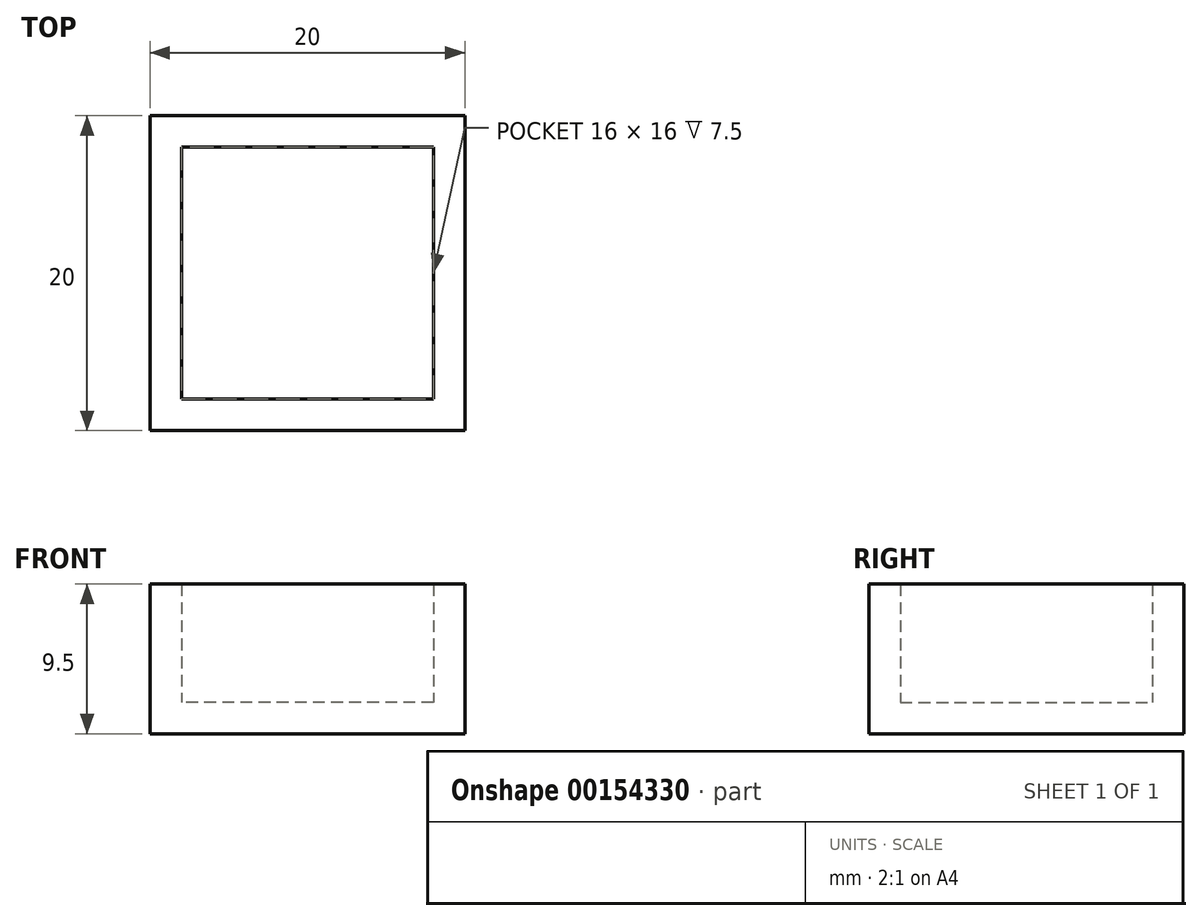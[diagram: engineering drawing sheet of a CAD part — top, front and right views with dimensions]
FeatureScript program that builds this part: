
annotation { "Feature Type Name" : "Feature", "Feature Type Description" : "" }
export const myFeature = defineFeature(function(context is Context, id is Id, definition is map)
    precondition{}
    {
        {
            var Q0;
            Q0=qCreatedBy(makeId("Top.planeOp"),FACE);
            var sketch = newSketch(context, id + "F0", { "sketchPlane" : qUnion([Q0])});
            skLineSegment(sketch, "E0.bottom", {"start": v(10, -10) * mm, "end": v(-10, -10) * mm});
            skLineSegment(sketch, "E0.top", {"start": v(10, 10) * mm, "end": v(-10, 10) * mm});
            skLineSegment(sketch, "E0.left", {"start": v(10, -10) * mm, "end": v(10, 10) * mm});
            skLineSegment(sketch, "E0.right", {"start": v(-10, -10) * mm, "end": v(-10, 10) * mm});
            skPoint(sketch, "E0.middle", {"position": v(0, 0) * mm});
            skLineSegment(sketch, "E1.0", {"start": v(-8, -8) * mm, "end": v(-8, 8) * mm});
            skLineSegment(sketch, "E1.1", {"start": v(8, -8) * mm, "end": v(-8, -8) * mm});
            skLineSegment(sketch, "E1.2", {"start": v(8, -8) * mm, "end": v(8, 8) * mm});
            skLineSegment(sketch, "E1.3", {"start": v(8, 8) * mm, "end": v(-8, 8) * mm});
            skSolve(sketch);
        }
        {
            var Q0;
            Q0=makeQuery(id+"F0.imprint","IMPRINT",FACE,{"disambiguationData":[TD([[makeQuery(id+"F0.imprint","IMPRINT",EDGE,{"derivedFrom":sQuery(id+"F0.wireOp",EDGE,"E0.bottom")}),-1.0]])]});
            extrude(context, id + "F1", {"entities" : qUnion([Q0]), "depth" : 9.5 * mm});
        }
        {
            var Q0;
            Q0=makeQuery(id+"F0.imprint","IMPRINT",FACE,{"disambiguationData":[TD([[makeQuery(id+"F0.imprint","IMPRINT",EDGE,{"derivedFrom":sQuery(id+"F0.wireOp",EDGE,"E1.0")}),-1.0]])]});
            extrude(context, id + "F2", {"entities" : qUnion([Q0]), "operationType" : NewBodyOperationType.ADD, "depth" : 2 * mm});
        }
    });
